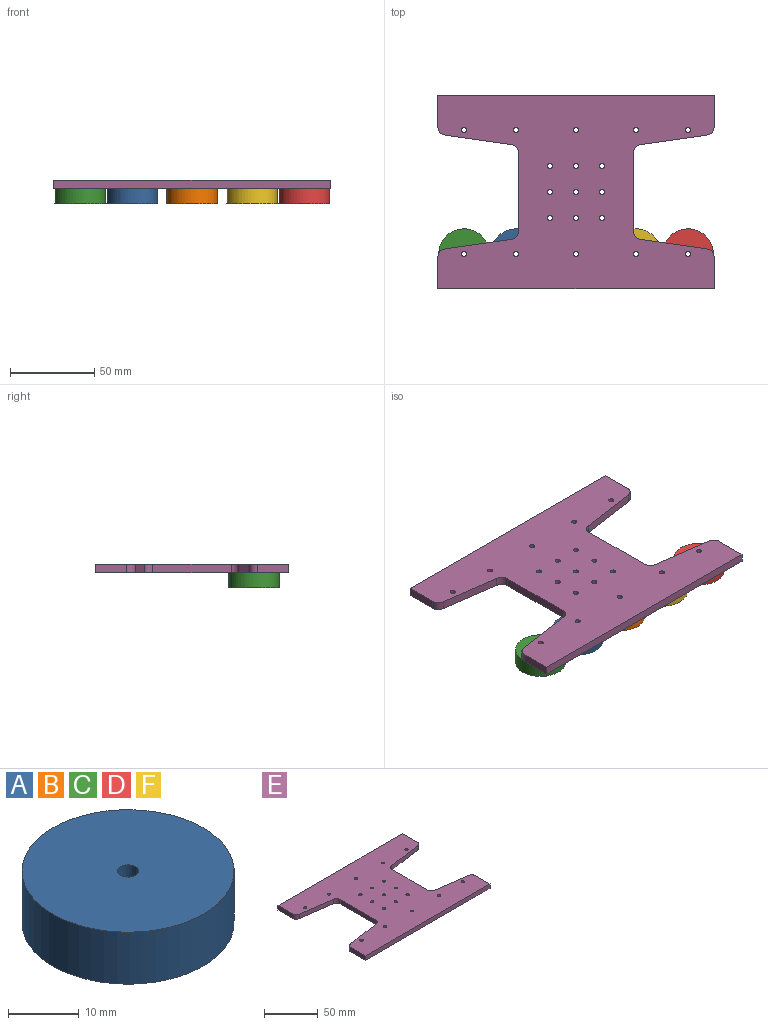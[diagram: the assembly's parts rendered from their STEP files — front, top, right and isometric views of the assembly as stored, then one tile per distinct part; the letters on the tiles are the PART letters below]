
ASSEMBLY  parts=6 mates=6
PART A: 4 faces, bbox 30x30x9 mm
  f0: cylinder r=1.5mm len=9mm, axis (0,0,-1), area 84.8mm2, adj f2,f3
  f1: cylinder r=15mm len=30mm, axis (0,0,-1), area 848.2mm2, adj f2,f3
  f2: plane 30x30mm, normal (0,0,1), area 699.8mm2, adj f0,f1
  f3: plane 30x30mm, normal (0,0,-1), area 699.8mm2, adj f0,f1
PART B: same geometry as A
PART C: same geometry as A
PART D: same geometry as A
PART E: 41 faces, bbox 164x114.7x5 mm
  f0: cylinder r=5mm len=5mm, axis (0,0,1), area 35.7mm2, adj f1,f22,f35,f36
  f1: plane 39.41x5.62mm, normal (0.14,0.99,0), area 199.1mm2, adj f0,f35,f36,f37
  f2: plane 18.66x5mm, normal (1,0,0), area 93.3mm2, adj f3,f35,f36,f37
  f3: plane 164x5mm, normal (0,-1,0), area 820mm2, adj f2,f4,f35,f36
  f4: plane 18.66x5mm, normal (-1,0,0), area 93.3mm2, adj f3,f35,f36,f38
  f5: plane 39.41x5.62mm, normal (-0.14,0.99,0), area 199.1mm2, adj f6,f35,f36,f38
  f6: cylinder r=5mm len=5mm, axis (0,0,1), area 35.7mm2, adj f5,f7,f35,f36
  f7: plane 46.33x5mm, normal (-1,0,0), area 231.6mm2, adj f6,f8,f35,f36
  f8: cylinder r=5mm len=5mm, axis (0,0,1), area 35.7mm2, adj f7,f9,f35,f36
  f9: plane 39.41x5.62mm, normal (-0.14,-0.99,0), area 199.1mm2, adj f8,f35,f36,f39
  f10: plane 18.66x5mm, normal (-1,0,0), area 93.3mm2, adj f11,f35,f36,f39
  f11: plane 164x5mm, normal (0,1,0), area 820mm2, adj f10,f12,f35,f36
  f12: plane 18.66x5mm, normal (1,0,0), area 93.3mm2, adj f11,f35,f36,f40
  f13: plane 39.41x5.62mm, normal (0.14,-0.99,0), area 199.1mm2, adj f14,f35,f36,f40
  f14: cylinder r=5mm len=5mm, axis (0,0,1), area 35.7mm2, adj f13,f22,f35,f36
  f15: cylinder r=1.5mm len=5mm, axis (0,0,1), area 47.1mm2, adj f35,f36
  f16: cylinder r=1.5mm len=5mm, axis (0,0,1), area 47.1mm2, adj f35,f36
  f17: cylinder r=1.5mm len=5mm, axis (0,0,1), area 47.1mm2, adj f35,f36
  f18: cylinder r=1.5mm len=5mm, axis (0,0,1), area 47.1mm2, adj f35,f36
  f19: cylinder r=1.5mm len=5mm, axis (0,0,1), area 47.1mm2, adj f35,f36
  f20: cylinder r=1.5mm len=5mm, axis (0,0,1), area 47.1mm2, adj f35,f36
  f21: cylinder r=1.5mm len=5mm, axis (0,0,1), area 47.1mm2, adj f35,f36
  f22: plane 46.33x5mm, normal (1,0,0), area 231.6mm2, adj f0,f14,f35,f36
  f23: cylinder r=1.5mm len=5mm, axis (0,0,1), area 47.1mm2, adj f35,f36
  f24: cylinder r=1.5mm len=5mm, axis (0,0,1), area 47.1mm2, adj f35,f36
  f25: cylinder r=1.5mm len=5mm, axis (0,0,1), area 47.1mm2, adj f35,f36
  f26: cylinder r=1.5mm len=5mm, axis (0,0,1), area 47.1mm2, adj f35,f36
  f27: cylinder r=1.5mm len=5mm, axis (0,0,1), area 47.1mm2, adj f35,f36
  f28: cylinder r=1.5mm len=5mm, axis (0,0,1), area 47.1mm2, adj f35,f36
  f29: cylinder r=1.5mm len=5mm, axis (0,0,1), area 47.1mm2, adj f35,f36
  f30: cylinder r=1.5mm len=5mm, axis (0,0,1), area 47.1mm2, adj f35,f36
  f31: cylinder r=1.5mm len=5mm, axis (0,0,1), area 47.1mm2, adj f35,f36
  f32: cylinder r=1.5mm len=5mm, axis (0,0,1), area 47.1mm2, adj f35,f36
  f33: cylinder r=1.5mm len=5mm, axis (0,0,1), area 47.1mm2, adj f35,f36
  f34: cylinder r=1.5mm len=5mm, axis (0,0,1), area 47.1mm2, adj f35,f36
  f35: plane 164x114.7mm, normal (0,0,-1), area 12738.9mm2, adj f0,f1,f2,f3,f4,f5,f6,f7
  f36: plane 164x114.7mm, normal (0,0,1), area 12738.9mm2, adj f0,f1,f2,f3,f4,f5,f6,f7
  f37: cylinder r=5mm len=5mm, axis (0,0,1), area 35.7mm2, adj f1,f2,f35,f36
  f38: cylinder r=5mm len=5mm, axis (0,0,-1), area 35.7mm2, adj f4,f5,f35,f36
  f39: cylinder r=5mm len=5mm, axis (0,0,1), area 35.7mm2, adj f9,f10,f35,f36
  f40: cylinder r=5mm len=5mm, axis (0,0,1), area 35.7mm2, adj f12,f13,f35,f36
PART F: same geometry as A
PLACE A t=(-35.5,20.5,-11.5)mm
PLACE B t=(0,20.5,-11.5)mm
PLACE C t=(-66.5,20.5,-11.5)mm
PLACE D t=(66.5,20.5,-11.5)mm
PLACE E t=(0,133.92,69.5)mm
PLACE F t=(35.5,20.5,-11.5)mm
MATE fastened E.f15 <-> C.f0  axis (0,0,-1) through (-66.5,20.5,-2.5)mm
MATE fastened E.f16 <-> A.f0  axis (0,0,-1) through (-35.5,20.5,-2.5)mm
MATE fastened B.f0 <-> E.f34  axis (0,0,1) through (0,20.5,-2.5)mm
MATE fastened F.f0 <-> E.f24  axis (0,0,1) through (35.5,20.5,-2.5)mm
MATE planar F.f0 <-> A.f0  axis (0,0,1) through (35.5,20.5,-2.5)mm
MATE fastened E.f17 <-> D.f0  axis (0,0,-1) through (66.5,20.5,-2.5)mm
